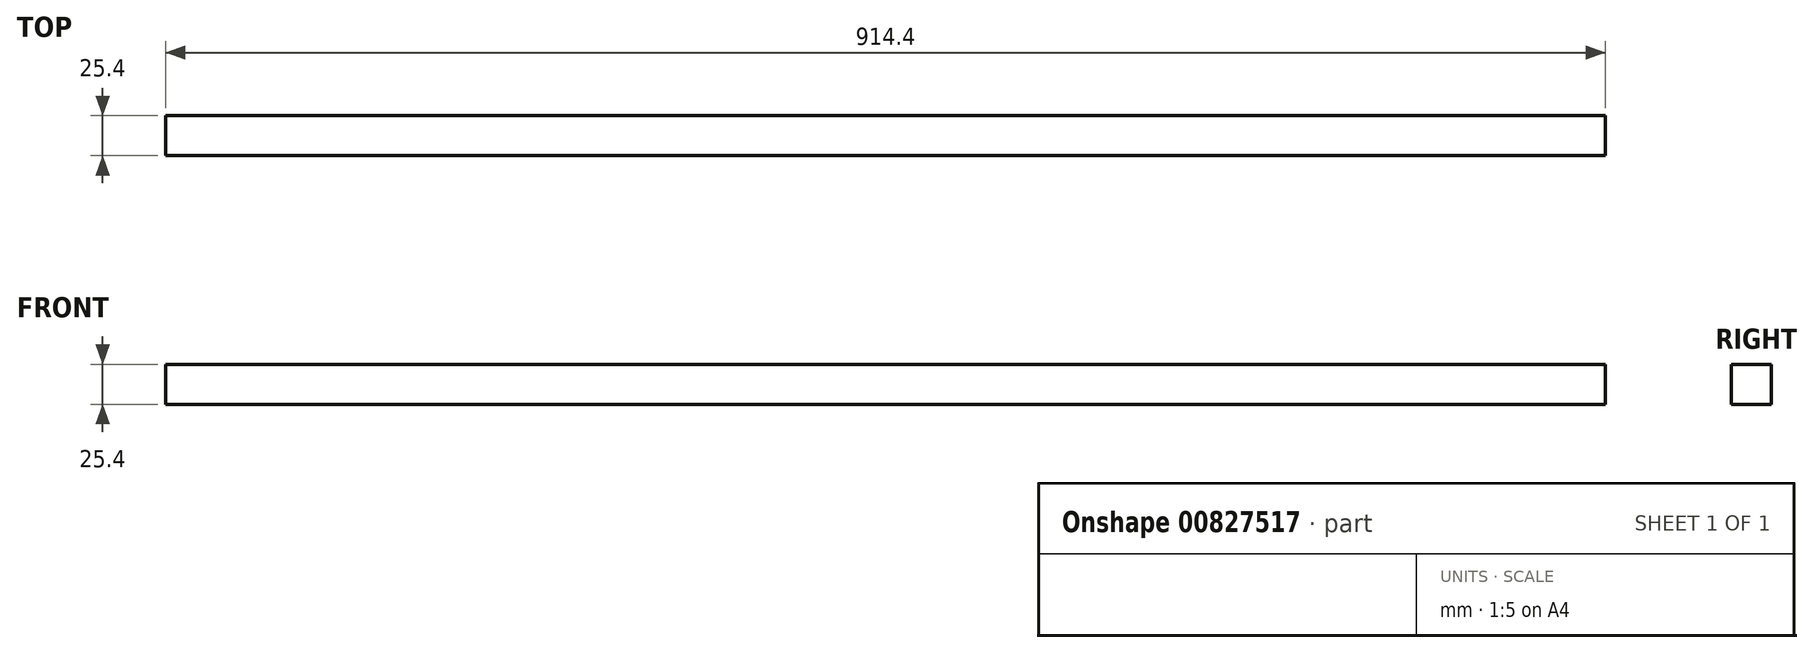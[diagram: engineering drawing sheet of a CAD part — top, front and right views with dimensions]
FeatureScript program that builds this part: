
annotation { "Feature Type Name" : "Feature", "Feature Type Description" : "" }
export const myFeature = defineFeature(function(context is Context, id is Id, definition is map)
    precondition{}
    {
        {
            var Q0;
            Q0=qCreatedBy(makeId("Front.planeOp"),FACE);
            var sketch = newSketch(context, id + "F0", { "sketchPlane" : qUnion([Q0])});
            skLineSegment(sketch, "E0", {"start": v(-457.2, 12.7) * mm, "end": v(-457.2, -12.7) * mm});
            skLineSegment(sketch, "E1", {"start": v(-457.2, 12.7) * mm, "end": v(457.2, 12.7) * mm});
            skLineSegment(sketch, "E2", {"start": v(-457.2, -12.7) * mm, "end": v(457.2, -12.7) * mm});
            skLineSegment(sketch, "E3", {"start": v(457.2, 12.7) * mm, "end": v(457.2, -12.7) * mm});
            skSolve(sketch);
        }
        {
            var Q0;
            Q0=makeQuery(id+"F0.imprint","IMPRINT",FACE,{"disambiguationData":[TD([[makeQuery(id+"F0.imprint","IMPRINT",EDGE,{"derivedFrom":sQuery(id+"F0.wireOp",EDGE,"E0")}),1.0]])]});
            extrude(context, id + "F1", {"entities" : qUnion([Q0]), "depth" : 25.4 * mm, "offsetDistance" : 25.4 * mm});
        }
    });
